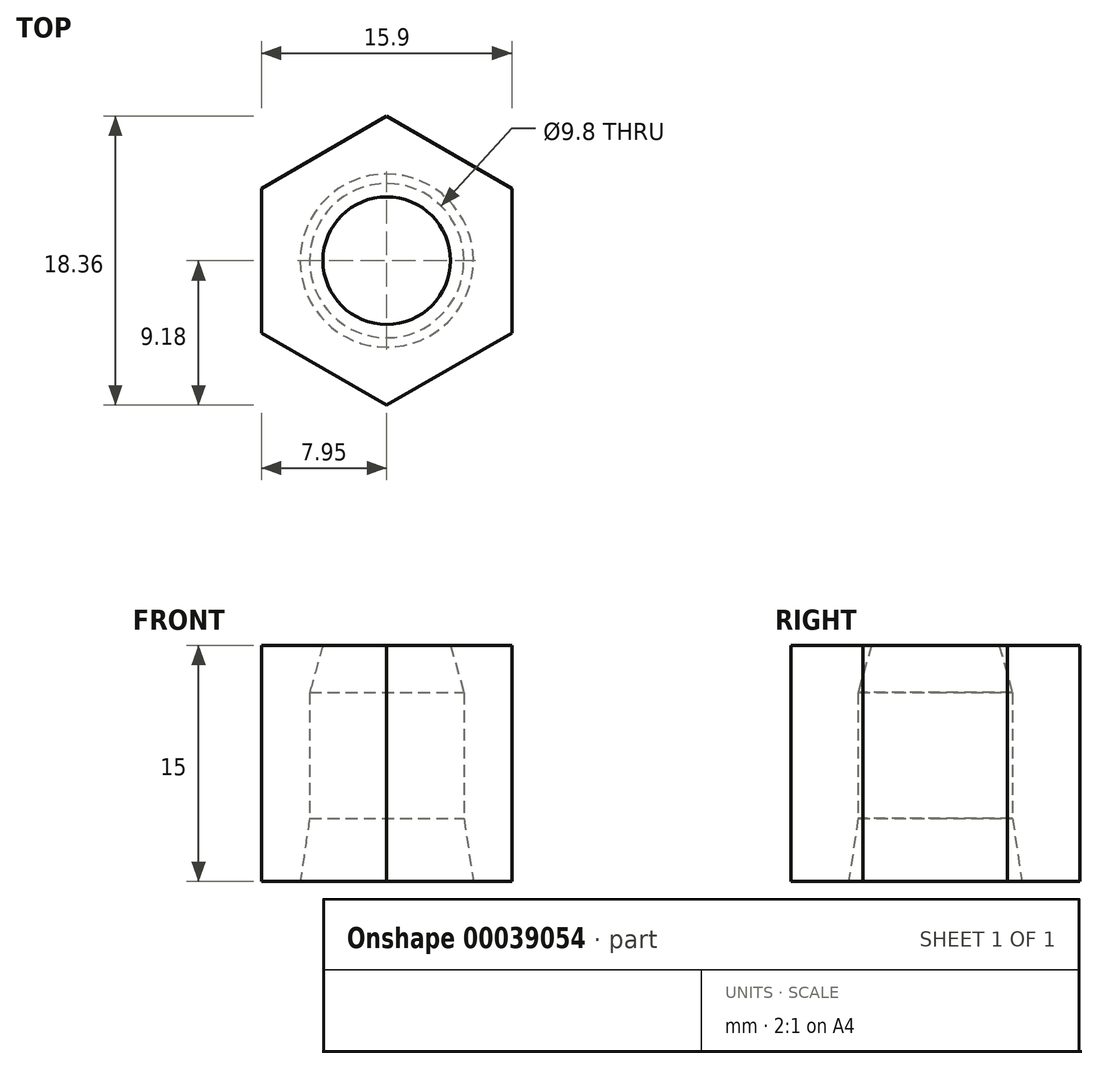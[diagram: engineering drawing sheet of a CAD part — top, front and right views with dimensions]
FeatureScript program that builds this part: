
annotation { "Feature Type Name" : "Feature", "Feature Type Description" : "" }
export const myFeature = defineFeature(function(context is Context, id is Id, definition is map)
    precondition{}
    {
        {
            var Q0;
            Q0=qCreatedBy(makeId("Front.planeOp"),FACE);
            var sketch = newSketch(context, id + "F0", { "sketchPlane" : qUnion([Q0])});
            skLineSegment(sketch, "E0", {"start": v(0, 0) * mm, "end": v(0, 14) * mm, "construction": true});
            skLineSegment(sketch, "E1", {"start": v(-4.9, 0) * mm, "end": v(-4.9, 8) * mm});
            skLineSegment(sketch, "E2", {"start": v(-4.9, 11) * mm, "end": v(-30, 11) * mm});
            skLineSegment(sketch, "E3", {"start": v(-30, 11) * mm, "end": v(-30, -4) * mm});
            skLineSegment(sketch, "E4", {"start": v(-30, -4) * mm, "end": v(-5.5, -4) * mm});
            skLineSegment(sketch, "E5", {"start": v(-5.5, -4) * mm, "end": v(-4.9, 0) * mm});
            skLineSegment(sketch, "E6", {"start": v(-4.9, 8) * mm, "end": v(-4.05, 11) * mm});
            skLineSegment(sketch, "E7", {"start": v(-4.05, 11) * mm, "end": v(-4.9, 11) * mm});
            skSolve(sketch);
        }
        {
            var Q0;
            Q0=makeQuery(id+"F0.imprint","IMPRINT",FACE,{"disambiguationData":[TD([[makeQuery(id+"F0.imprint","IMPRINT",EDGE,{"derivedFrom":sQuery(id+"F0.wireOp",EDGE,"E1")}),1.0]])]});
            var Q1;
            Q1=sQuery(id+"F0.wireOp",EDGE,"E0");
            revolve(context, id + "F1", {"entities" : qUnion([Q0]), "axis" : qUnion([Q1]), "revolveType" : RevolveType.FULL});
        }
        {
            var Q0;
            Q0=makeQuery(id+"F1.opRevolve","SWEPT_FACE",FACE,{"disambiguationData":[OSD([sQuery(id+"F0.wireOp",EDGE,"E2")])]});
            var sketch = newSketch(context, id + "F2", { "sketchPlane" : qUnion([Q0])});
            skCircle(sketch, "E8.cCircle", {"center": v(0, 0) * mm, "radius": 7.95 * mm, "construction": true});
            skLineSegment(sketch, "E8.0", {"start": v(7.95, 4.59) * mm, "end": v(7.95, -4.59) * mm});
            skLineSegment(sketch, "E8.1", {"start": v(7.95, -4.59) * mm, "end": v(0, -9.18) * mm});
            skLineSegment(sketch, "E8.2", {"start": v(0, -9.18) * mm, "end": v(-7.95, -4.59) * mm});
            skLineSegment(sketch, "E8.3", {"start": v(-7.95, -4.59) * mm, "end": v(-7.95, 4.59) * mm});
            skLineSegment(sketch, "E8.4", {"start": v(-7.95, 4.59) * mm, "end": v(0, 9.18) * mm});
            skLineSegment(sketch, "E8.5", {"start": v(0, 9.18) * mm, "end": v(7.95, 4.59) * mm});
            skPoint(sketch, "E8.0.midPoint", {"position": v(7.95, 0) * mm});
            skCircle(sketch, "E9.0", {"center": v(0, 0) * mm, "radius": 30 * mm});
            skSolve(sketch);
        }
        {
            var Q0;
            Q0=makeQuery(id+"F2.imprint","IMPRINT",FACE,{"disambiguationData":[TD([[makeQuery(id+"F2.imprint","IMPRINT",EDGE,{"derivedFrom":sQuery(id+"F2.wireOp",EDGE,"E8.0")}),1.0]])]});
            extrude(context, id + "F3", {"entities" : qUnion([Q0]), "operationType" : NewBodyOperationType.REMOVE, "endBound" : BoundingType.THROUGH_ALL, "oppositeDirection" : true, "depth" : 25 * mm});
        }
    });
